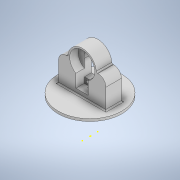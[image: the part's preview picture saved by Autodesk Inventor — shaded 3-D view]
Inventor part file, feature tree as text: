
AUTODESK INVENTOR PART (.ipt)
format: ipt  version: 2021 (Build 250183000, 183)  size: 395,264 bytes
history: native  units: mm
features: sketch x58, extrude x28, plane x11, fillet x4
ambient origin geometry x8: Origin, YZ Plane, XZ Plane, XY Plane, X Axis, Y Axis, Z Axis, Center Point
bodies: Solid1 (feature_tree)
feature tree (101):
  sketch  "Sketch1"  dims[d12=105.0mm d13=4.0mm d14=0.0mm]
  plane  "Work Plane26"
  plane  "Work Plane42"
  extrude  "Extrusion5"  Depth=4.0mm TaperAngle=0.0deg
  plane  "Work Plane34"
  extrude  "Extrusion6"  Depth=4.5mm TaperAngle=0.0deg
  plane  "Work Plane33"
  extrude  "Extrusion7"  TaperAngle=0.0deg  [1 undecoded]
  plane  "Work Plane30"
  sketch  "Sketch10"  dims[d18=4.0mm d19=0.0mm d66=0.0mm]
  plane  "Work Plane31"
  sketch  "Sketch11"  dims[d93=46.75mm d94=0.0mm d95=25.5634mm d96=0.0mm]
  sketch  "Sketch13"  dims[d102=20.0mm d103=41.0mm]
  plane  "Work Plane35"
  sketch  "Sketch18"  dims[d104=11.995mm d105=0.0mm d110=6.7mm]
  sketch  "Sketch19"  dims[d111=6.7mm d112=10.0mm]
  sketch  "Sketch32"  dims[d113=10.0mm d114=5.0mm d115=5.0mm d116=29.0mm d117=0.0mm]
  sketch  "Sketch33"  dims[d118=10.0mm d119=10.0mm]
  sketch  "Sketch34"  dims[d120=5.0mm d121=5.0mm]
  sketch  "Sketch35"  dims[d122=41.75mm d123=0.0mm d270=13.0mm]
  plane  "Work Plane3"
  extrude  "Extrusion27"  Depth=25.5634mm TaperAngle=0.0deg
  plane  "Work Plane41"
  extrude  "Extrusion28"  Depth=41.495mm TaperAngle=0.0deg
  sketch  "Sketch57"  dims[d283=14.0mm d284=0.0mm d285=14.0mm d286=0.0mm]
  sketch  "Sketch58"  dims[d287=40.5mm d288=0.0mm d289=40.5mm d290=20.25mm d291=0.0mm d292=0.0mm]
  sketch  "Sketch59"  dims[d293=40.5mm d294=0.0mm d295=21.75mm d296=0.0mm]
  sketch  "Sketch61"  dims[d297=40.5mm d298=21.75mm d299=0.0mm d300=2.0mm d301=2.0mm]
  extrude  "Extrusion30"  Depth=41.0mm
  sketch  "Sketch63"  dims[d305=14.5mm d306=0.0mm d307=14.0mm d308=0.0mm]
  extrude  "Extrusion29"  Depth=6.7mm
  sketch  "Sketch64"  dims[d309=5.5mm d310=4.6mm]
  plane  "Work Plane4"
  plane  "Work Plane40"
  sketch  "Sketch68"  dims[d311=14.0mm d312=0.0mm d313=14.0mm d314=0.0mm]
  sketch  "Sketch69"  dims[d315=14.0mm d316=0.0mm d317=5.5mm]
  sketch  "Sketch70"  dims[d318=5.0mm d319=14.0mm d320=0.0mm]
  sketch  "Sketch71"  dims[d321=14.5mm d322=0.0mm d323=14.0mm d324=0.0mm]
  sketch  "Sketch72"  dims[d325=5.2mm d326=4.7mm]
  extrude  "Extrusion33"  Depth=10.0mm
  sketch  "Sketch73"  dims[d327=14.0mm d328=0.0mm d9=0.5mm]
  extrude  "Extrusion34"  Depth=10.0mm
  fillet  "Fillet8"  Radius=5.0mm
  fillet  "Fillet9"  Radius=29.0mm
  extrude  "Extrusion64"  Depth=10.0mm
  sketch  "Sketch135"  dims[d30=0.872665mm]
  sketch  "Sketch136"  dims[d31=0.5mm]
  extrude  "Extrusion65"  Depth=5.0mm
  sketch  "Sketch140"  dims[d53=0.5mm]
  extrude  "Extrusion68"  Depth=13.0mm
  extrude  "Extrusion69"  Depth=13.0mm
  extrude  "Extrusion70"  Depth=14.0mm TaperAngle=0.0deg
  extrude  "Extrusion71"  Depth=14.0mm TaperAngle=0.0deg
  extrude  "Extrusion72"  Depth=40.5mm TaperAngle=0.0deg
  extrude  "Extrusion73"  Depth=40.5mm TaperAngle=0.0deg
  extrude  "Extrusion74"  Depth=2.0mm TaperAngle=0.0deg
  fillet  "Fillet10"  Radius=2.0mm
  fillet  "Fillet11"  Radius=2.0mm
  sketch  "Sketch149"  dims[d62=0.872665mm]
  sketch  "Sketch150"  dims[d69=0.5mm]
  extrude  "Extrusion75"  Depth=14.0mm TaperAngle=0.0deg
  sketch  "Sketch152"  dims[d71=0.5mm]
  sketch  "Sketch153"  dims[d72=0.872665mm]
  sketch  "Sketch154"  dims[d125=0.5mm]
  extrude  "Extrusion76"  Depth=14.0mm TaperAngle=0.0deg
  extrude  "Extrusion77"  Depth=4.6mm
  sketch  "Sketch157"  dims[d128=0.872665mm]
  extrude  "Extrusion78"  Depth=14.0mm TaperAngle=0.0deg
  sketch  "Sketch159"  dims[d130=0.5mm]
  extrude  "Extrusion79"  Depth=14.0mm
  extrude  "Extrusion80"  Depth=14.0mm TaperAngle=0.0deg
  extrude  "Extrusion81"  Depth=14.0mm TaperAngle=0.0deg
  extrude  "Extrusion82"  Depth=4.7mm
  extrude  "Extrusion83"  Depth=14.0mm
  extrude  "Extrusion84"  Depth=0.5mm
  sketch  "Sketch166"  dims[d140=0.872665mm]
  sketch  "Sketch167"  dims[d141=0.5mm d142=0.872665mm d173=0.5mm d174=0.872665mm d175=0.5mm d176=0.872665mm d177=0.5mm d178=0.872665mm d179=0.5mm d180=0.872665mm d182=0.5mm d183=0.872665mm d184=0.5mm d185=0.872665mm d197=0.5mm d198=0.872665mm d199=0.5mm d200=0.872665mm d228=0.5mm d229=0.872665mm d230=0.5mm d231=0.872665mm d238=0.5mm d239=0.872665mm d240=0.5mm d241=0.872665mm]
  sketch  "Sketch8"  dims[d15=102.0mm d16=4.5mm d17=0.0mm]
  sketch  "Sketch12"  dims[d99=21.0mm d100=41.495mm d101=0.0mm]
  sketch  "Sketch55"  dims[d271=13.0mm d272=5.0mm]
  sketch  "Sketch56"  dims[d273=14.0mm d274=0.0mm d275=10.25mm d276=0.0mm]
  sketch  "Sketch62"  dims[d302=5.2mm d303=14.0mm d304=0.0mm]
  sketch  "Sketch75"  dims[d10=0.872665mm d11=0.5mm]
  sketch  "Sketch134"  dims[d29=0.5mm]
  sketch  "Sketch137"  dims[d32=0.872665mm]
  sketch  "Sketch142"  dims[d54=0.872665mm]
  sketch  "Sketch143"  dims[d55=0.5mm]
  sketch  "Sketch144"  dims[d56=0.872665mm]
  sketch  "Sketch145"  dims[d59=0.5mm]
  sketch  "Sketch147"  dims[d60=0.872665mm]
  sketch  "Sketch148"  dims[d61=0.5mm]
  sketch  "Sketch151"  dims[d70=0.872665mm]
  sketch  "Sketch155"  dims[d126=0.872665mm]
  sketch  "Sketch156"  dims[d127=0.5mm]
  sketch  "Sketch158"  dims[d129=0.872665mm]
  sketch  "Sketch160"  dims[d131=0.872665mm]
  sketch  "Sketch161"  dims[d135=0.5mm]
  sketch  "Sketch162"  dims[d136=0.872665mm]
  sketch  "Sketch163"  dims[d137=0.5mm]
  sketch  "Sketch164"  dims[d138=0.872665mm]
  sketch  "Sketch165"  dims[d139=0.5mm]
note: 1 required parameter value undecoded (feature->parameter linkage not recoverable at this tier; creation-order binding heuristic only, values carry confidence <= 0.55)
